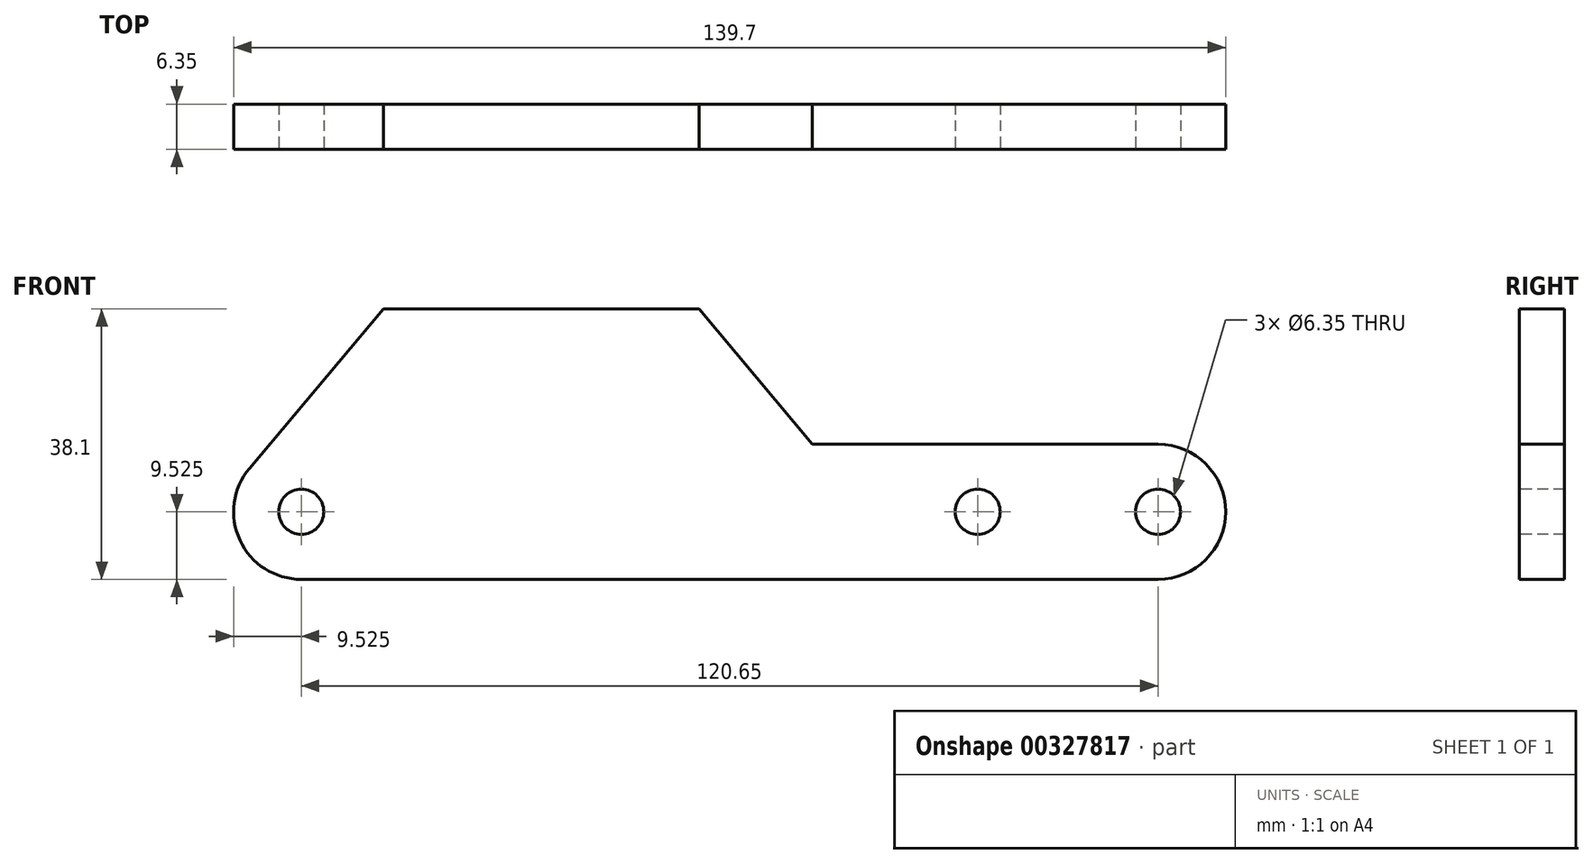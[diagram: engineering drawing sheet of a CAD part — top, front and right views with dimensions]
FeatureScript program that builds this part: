
annotation { "Feature Type Name" : "Feature", "Feature Type Description" : "" }
export const myFeature = defineFeature(function(context is Context, id is Id, definition is map)
    precondition{}
    {
        {
            var Q0;
            Q0=qCreatedBy(makeId("Front.planeOp"),FACE);
            var sketch = newSketch(context, id + "F0", { "sketchPlane" : qUnion([Q0])});
            skLineSegment(sketch, "E0.bottom", {"start": v(0, 0) * mm, "end": v(139.7, 0) * mm});
            skLineSegment(sketch, "E0.top", {"start": v(0, 19.05) * mm, "end": v(139.7, 19.05) * mm});
            skLineSegment(sketch, "E0.left", {"start": v(0, 0) * mm, "end": v(0, 19.05) * mm});
            skLineSegment(sketch, "E0.right", {"start": v(139.7, 0) * mm, "end": v(139.7, 19.05) * mm});
            skSolve(sketch);
        }
        {
            var Q0;
            Q0 = qSketchRegion(id + "F0", true);
            extrude(context, id + "F1", {"entities" : qUnion([Q0]), "depth" : 6.35 * mm});
        }
        {
            var Q0;
            Q0=makeQuery(id+"F1.opExtrude","CAP_FACE",FACE,{"disambiguationData":[OSD([sQuery(id+"F0.wireOp",EDGE,"E0.bottom"),sQuery(id+"F0.wireOp",EDGE,"E0.top"),sQuery(id+"F0.wireOp",EDGE,"E0.left"),sQuery(id+"F0.wireOp",EDGE,"E0.right")])],"isStart":false});
            var sketch = newSketch(context, id + "F2", { "sketchPlane" : qUnion([Q0])});
            skCircle(sketch, "E1", {"center": v(130.18, 9.53) * mm, "radius": 3.18 * mm});
            skSolve(sketch);
        }
        {
            var Q0;
            Q0 = qSketchRegion(id + "F2", true);
            extrude(context, id + "F3", {"entities" : qUnion([Q0]), "operationType" : NewBodyOperationType.REMOVE, "endBound" : BoundingType.THROUGH_ALL, "oppositeDirection" : true, "depth" : 25.4 * mm});
        }
        {
            var Q0;
            Q0=makeQuery(id+"F1.opExtrude","CAP_FACE",FACE,{"disambiguationData":[OSD([sQuery(id+"F0.wireOp",EDGE,"E0.bottom"),sQuery(id+"F0.wireOp",EDGE,"E0.top"),sQuery(id+"F0.wireOp",EDGE,"E0.left"),sQuery(id+"F0.wireOp",EDGE,"E0.right")])],"isStart":false});
            var sketch = newSketch(context, id + "F4", { "sketchPlane" : qUnion([Q0])});
            skCircle(sketch, "E2", {"center": v(104.78, 9.53) * mm, "radius": 3.17 * mm});
            skCircle(sketch, "E3.0", {"center": v(130.18, 9.53) * mm, "radius": 3.18 * mm, "construction": true});
            skSolve(sketch);
        }
        {
            var Q0;
            Q0 = qSketchRegion(id + "F4", true);
            extrude(context, id + "F5", {"entities" : qUnion([Q0]), "operationType" : NewBodyOperationType.REMOVE, "oppositeDirection" : true, "depth" : 25.4 * mm});
        }
        {
            var Q0;
            Q0=makeQuery(id+"F1.opExtrude","SWEPT_EDGE",EDGE,{"disambiguationData":[OSD([sQuery(id+"F0.wireOp",EDGE,"E0.top"),sQuery(id+"F0.wireOp",EDGE,"E0.right")])]});
            var Q1;
            Q1=makeQuery(id+"F1.opExtrude","SWEPT_EDGE",EDGE,{"disambiguationData":[OSD([sQuery(id+"F0.wireOp",EDGE,"E0.bottom"),sQuery(id+"F0.wireOp",EDGE,"E0.right")])]});
            fillet(context, id + "F6", {"entities" : qUnion([Q0, Q1]), "radius" : 9.52 * mm, "tangentPropagation" : true, "allowEdgeOverflow" : false});
        }
        {
            var Q0;
            Q0=makeQuery(id+"F1.opExtrude","SWEPT_EDGE",EDGE,{"disambiguationData":[OSD([sQuery(id+"F0.wireOp",EDGE,"E0.top"),sQuery(id+"F0.wireOp",EDGE,"E0.left")])]});
            var Q1;
            Q1=makeQuery(id+"F1.opExtrude","SWEPT_EDGE",EDGE,{"disambiguationData":[OSD([sQuery(id+"F0.wireOp",EDGE,"E0.bottom"),sQuery(id+"F0.wireOp",EDGE,"E0.left")])]});
            fillet(context, id + "F7", {"entities" : qUnion([Q0, Q1]), "radius" : 9.52 * mm, "tangentPropagation" : true, "allowEdgeOverflow" : false});
        }
        {
            var Q0;
            Q0=makeQuery(id+"F1.opExtrude","CAP_FACE",FACE,{"disambiguationData":[OSD([sQuery(id+"F0.wireOp",EDGE,"E0.bottom"),sQuery(id+"F0.wireOp",EDGE,"E0.top"),sQuery(id+"F0.wireOp",EDGE,"E0.left"),sQuery(id+"F0.wireOp",EDGE,"E0.right")])],"isStart":false});
            var sketch = newSketch(context, id + "F8", { "sketchPlane" : qUnion([Q0])});
            skCircle(sketch, "E4", {"center": v(9.53, 9.52) * mm, "radius": 3.17 * mm});
            skSolve(sketch);
        }
        {
            var Q0;
            Q0 = qSketchRegion(id + "F8", true);
            extrude(context, id + "F9", {"entities" : qUnion([Q0]), "operationType" : NewBodyOperationType.REMOVE, "endBound" : BoundingType.THROUGH_ALL, "oppositeDirection" : true, "depth" : 25.4 * mm});
        }
        {
            var Q0;
            Q0=makeQuery(id+"F1.opExtrude","CAP_FACE",FACE,{"disambiguationData":[OSD([sQuery(id+"F0.wireOp",EDGE,"E0.bottom"),sQuery(id+"F0.wireOp",EDGE,"E0.top"),sQuery(id+"F0.wireOp",EDGE,"E0.left"),sQuery(id+"F0.wireOp",EDGE,"E0.right")])],"isStart":false});
            var sketch = newSketch(context, id + "F10", { "sketchPlane" : qUnion([Q0])});
            skLineSegment(sketch, "E5", {"start": v(2.23, 15.65) * mm, "end": v(21.07, 38.1) * mm});
            skLineSegment(sketch, "E6", {"start": v(21.07, 38.1) * mm, "end": v(65.52, 38.1) * mm});
            skLineSegment(sketch, "E7", {"start": v(65.52, 38.1) * mm, "end": v(81.5, 19.05) * mm});
            skLineSegment(sketch, "E8", {"start": v(81.5, 19.05) * mm, "end": v(9.52, 19.05) * mm});
            skArc(sketch, "E9.0", {"start": v(9.53, 19.05) * mm, "mid": v(5.5, 18.16) * mm, "end": v(2.23, 15.65) * mm});
            skPoint(sketch, "E10.orphan", {"position": v(9.53, 0) * mm});
            skSolve(sketch);
        }
        {
            var Q0;
            Q0 = qSketchRegion(id + "F10", true);
            extrude(context, id + "F11", {"entities" : qUnion([Q0]), "operationType" : NewBodyOperationType.ADD, "oppositeDirection" : true, "depth" : 6.35 * mm});
        }
    });
